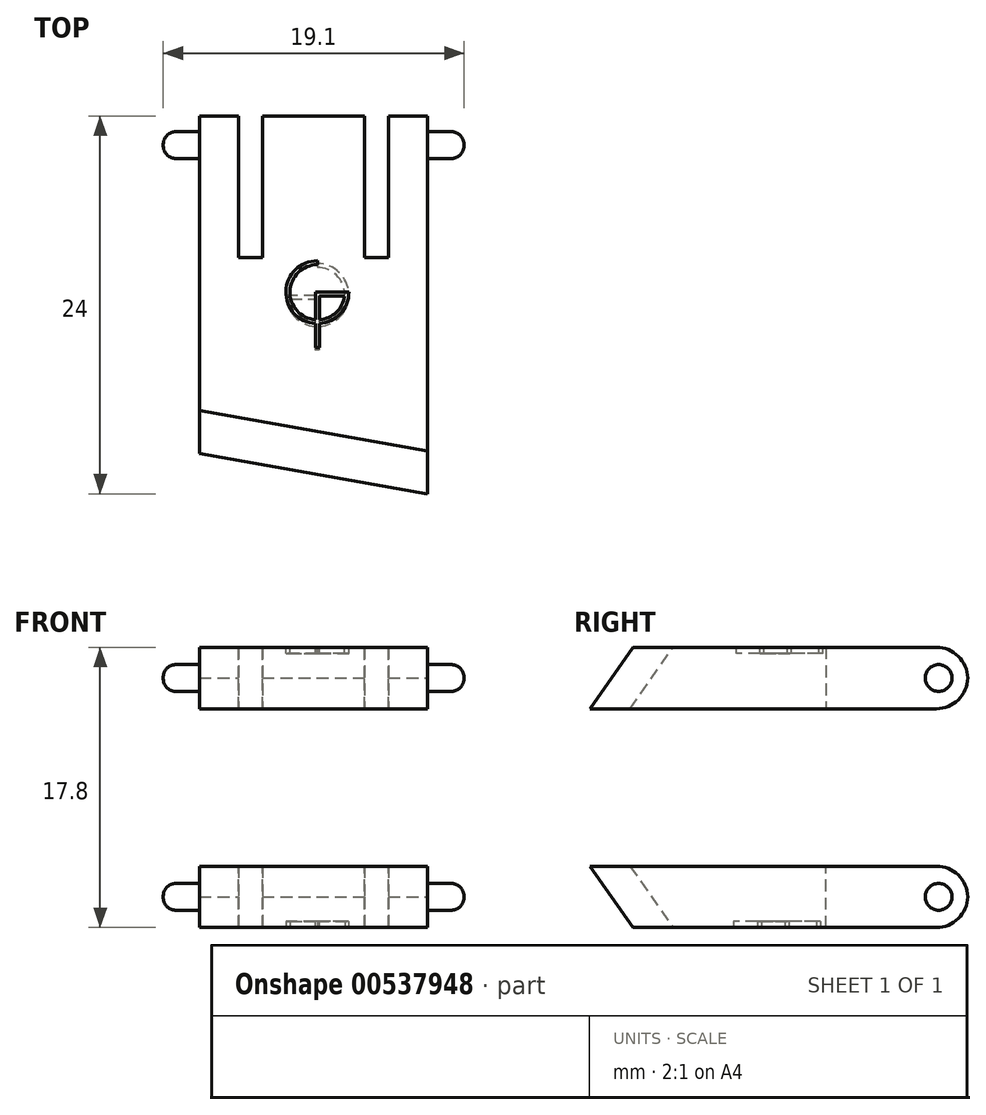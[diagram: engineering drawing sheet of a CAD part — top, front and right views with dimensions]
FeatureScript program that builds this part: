
annotation { "Feature Type Name" : "Feature", "Feature Type Description" : "" }
export const myFeature = defineFeature(function(context is Context, id is Id, definition is map)
    precondition{}
    {
        {
            var Q0;
            Q0=qCreatedBy(makeId("Top.planeOp"),FACE);
            var sketch = newSketch(context, id + "F0", { "sketchPlane" : qUnion([Q0])});
            skLineSegment(sketch, "E0", {"start": v(0, 0) * mm, "end": v(-14.5, 2.56) * mm});
            skLineSegment(sketch, "E1", {"start": v(-14.5, 2.56) * mm, "end": v(-14.5, 24) * mm});
            skLineSegment(sketch, "E2", {"start": v(-14.5, 24) * mm, "end": v(0, 24) * mm});
            skLineSegment(sketch, "E3", {"start": v(0, 24) * mm, "end": v(0, 0) * mm});
            skLineSegment(sketch, "E4.bottom", {"start": v(-12, 24) * mm, "end": v(-10.5, 24) * mm});
            skLineSegment(sketch, "E4.top", {"start": v(-12, 15) * mm, "end": v(-10.5, 15) * mm});
            skLineSegment(sketch, "E4.left", {"start": v(-12, 24) * mm, "end": v(-12, 15) * mm});
            skLineSegment(sketch, "E4.right", {"start": v(-10.5, 24) * mm, "end": v(-10.5, 15) * mm});
            skLineSegment(sketch, "E5.bottom", {"start": v(-2.5, 24) * mm, "end": v(-4, 24) * mm});
            skLineSegment(sketch, "E5.top", {"start": v(-2.5, 15) * mm, "end": v(-4, 15) * mm});
            skLineSegment(sketch, "E5.left", {"start": v(-2.5, 24) * mm, "end": v(-2.5, 15) * mm});
            skLineSegment(sketch, "E5.right", {"start": v(-4, 24) * mm, "end": v(-4, 15) * mm});
            skSolve(sketch);
        }
        {
            var Q0;
            Q0=makeQuery(id+"F0.imprint","IMPRINT",FACE,{"disambiguationData":[TD([[makeQuery(id+"F0.imprint","IMPRINT",EDGE,{"derivedFrom":sQuery(id+"F0.wireOp",EDGE,"E0")}),-1.0]])]});
            var Q1;
            {var subQ1=sQuery(id+"F0.wireOp",EDGE,"c5bb8d40-925b-485c-b122-8afd0081a890");Q1=makeQuery(id+"F0.imprint","IMPRINT",FACE,{"disambiguationData":[TD([[makeQuery(id+"F0.imprint","IMPRINT",EDGE,{"derivedFrom":subQ1}),1.0]])]});}
            var Q2;
            {var subQ0=sQuery(id+"F0.wireOp",EDGE,"f95112e1-4d56-459a-80a0-04d841074a68");Q2=makeQuery(id+"F0.imprint","IMPRINT",FACE,{"disambiguationData":[TD([[makeQuery(id+"F0.imprint","IMPRINT",EDGE,{"derivedFrom":subQ0}),1.0]])]});}
            var Q3;
            {var subQ1=sQuery(id+"F0.wireOp",EDGE,"91befa4d-aa7f-4066-8ede-e3ff8ab19f0f");Q3=makeQuery(id+"F0.imprint","IMPRINT",FACE,{"disambiguationData":[TD([[makeQuery(id+"F0.imprint","IMPRINT",EDGE,{"derivedFrom":subQ1}),1.0]])]});}
            var Q4;
            {var subQ5=sQuery(id+"F0.wireOp",EDGE,"8b45276f-696a-430b-a867-6ecf755f5e75");Q4=makeQuery(id+"F0.imprint","IMPRINT",FACE,{"disambiguationData":[TD([[makeQuery(id+"F0.imprint","IMPRINT",EDGE,{"derivedFrom":subQ5}),1.0]])]});}
            var Q5;
            {var subQ0=sQuery(id+"F0.wireOp",EDGE,"857528f7-3fc0-4300-9383-177ff648e449");var subQ1=sQuery(id+"F0.wireOp",EDGE,"b7ffc7d4-f97f-4348-9500-127a82e465bb");var subQ2=makeQuery(id+"F0.imprint","INTERSECT",VERTEX,{"derivedFrom":[subQ1,subQ0]});Q5=makeQuery(id+"F0.imprint","IMPRINT",FACE,{"disambiguationData":[TD([[makeQuery(id+"F0.imprint","IMPRINT",EDGE,{"disambiguationData":[TD([[subQ2,-1.0]])],"derivedFrom":subQ1}),1.0]])]});}
            var Q6;
            {var subQ0=sQuery(id+"F0.wireOp",EDGE,"2bfb2500-52ae-434e-aba9-8a9b67f69133");Q6=makeQuery(id+"F0.imprint","IMPRINT",FACE,{"disambiguationData":[TD([[makeQuery(id+"F0.imprint","IMPRINT",EDGE,{"derivedFrom":subQ0}),-1.0]])]});}
            extrude(context, id + "F1", {"entities" : qUnion([Q0, Q1, Q2, Q3, Q4, Q5, Q6]), "depth" : 3.9 * mm, "offsetDistance" : 25 * mm});
        }
        {
            var Q0;
            Q0=makeQuery(id+"F1.opExtrude","SWEPT_FACE",FACE,{"disambiguationData":[OSD([sQuery(id+"F0.wireOp",EDGE,"E3")])]});
            var sketch = newSketch(context, id + "F2", { "sketchPlane" : qUnion([Q0])});
            skCircle(sketch, "E6", {"center": v(22.15, 1.95) * mm, "radius": 0.85 * mm});
            skPoint(sketch, "E6.centerSnap0", {"position": v(24, 1.95) * mm});
            skSolve(sketch);
        }
        {
            var Q0;
            Q0 = qSketchRegion(id + "F2", true);
            extrude(context, id + "F3", {"entities" : qUnion([Q0]), "operationType" : NewBodyOperationType.ADD, "depth" : 2.3 * mm, "offsetDistance" : 25 * mm});
        }
        {
            var Q0;
            Q0=makeQuery(id+"F1.opExtrude","SWEPT_FACE",FACE,{"disambiguationData":[OSD([sQuery(id+"F0.wireOp",EDGE,"E1")])]});
            var sketch = newSketch(context, id + "F4", { "sketchPlane" : qUnion([Q0])});
            skCircle(sketch, "E7", {"center": v(-22.15, 1.95) * mm, "radius": 0.85 * mm});
            skPoint(sketch, "E7.centerSnap0", {"position": v(-24, 1.95) * mm});
            skSolve(sketch);
        }
        {
            var Q0;
            Q0=makeQuery(id+"F4.imprint","IMPRINT",FACE,{"disambiguationData":[TD([[makeQuery(id+"F4.imprint","IMPRINT",EDGE,{"derivedFrom":sQuery(id+"F4.wireOp",EDGE,"E7")}),1.0]])]});
            extrude(context, id + "F5", {"entities" : qUnion([Q0]), "operationType" : NewBodyOperationType.ADD, "depth" : 2.3 * mm, "offsetDistance" : 25 * mm});
        }
        {
            var Q0;
            Q0=makeQuery(id+"F3.opExtrude","CAP_FACE",FACE,{"disambiguationData":[OSD([sQuery(id+"F2.wireOp",EDGE,"E6")])],"isStart":false});
            var Q1;
            Q1=makeQuery(id+"F5.opExtrude","CAP_FACE",FACE,{"disambiguationData":[OSD([sQuery(id+"F4.wireOp",EDGE,"E7")])],"isStart":false});
            fillet(context, id + "F6", {"entities" : qUnion([Q0, Q1]), "radius" : .8 * mm, "allowEdgeOverflow" : false});
        }
        {
            var Q0;
            {var subQ0=sQuery(id+"F0.wireOp",EDGE,"E2");Q0=makeQuery(id+"F1.opExtrude","CAP_EDGE",EDGE,{"disambiguationData":[OSD([subQ0]),TDD([makeQuery(id+"F0.imprint","IMPRINT",EDGE,{"disambiguationData":[TD([[makeQuery(id+"F0.imprint","INTERSECT",VERTEX,{"derivedFrom":[subQ0,sQuery(id+"F0.wireOp",EDGE,"E4.bottom"),sQuery(id+"F0.wireOp",EDGE,"E4.right")]}),-1.0]])],"derivedFrom":subQ0})])],"isStart":false});}
            var Q1;
            {var subQ0=sQuery(id+"F0.wireOp",EDGE,"E2");Q1=makeQuery(id+"F1.opExtrude","CAP_EDGE",EDGE,{"disambiguationData":[OSD([subQ0]),TDD([makeQuery(id+"F0.imprint","IMPRINT",EDGE,{"disambiguationData":[TD([[makeQuery(id+"F0.imprint","INTERSECT",VERTEX,{"derivedFrom":[sQuery(id+"F0.wireOp",EDGE,"E1"),subQ0]}),-1.0]])],"derivedFrom":subQ0})])],"isStart":false});}
            var Q2;
            {var subQ0=sQuery(id+"F0.wireOp",EDGE,"E2");Q2=makeQuery(id+"F1.opExtrude","CAP_EDGE",EDGE,{"disambiguationData":[OSD([subQ0]),TDD([makeQuery(id+"F0.imprint","IMPRINT",EDGE,{"disambiguationData":[TD([[makeQuery(id+"F0.imprint","INTERSECT",VERTEX,{"derivedFrom":[subQ0,sQuery(id+"F0.wireOp",EDGE,"E3")]}),1.0]])],"derivedFrom":subQ0})])],"isStart":false});}
            var Q3;
            {var subQ0=sQuery(id+"F0.wireOp",EDGE,"E2");Q3=makeQuery(id+"F1.opExtrude","CAP_EDGE",EDGE,{"disambiguationData":[OSD([subQ0]),TDD([makeQuery(id+"F0.imprint","IMPRINT",EDGE,{"disambiguationData":[TD([[makeQuery(id+"F0.imprint","INTERSECT",VERTEX,{"derivedFrom":[subQ0,sQuery(id+"F0.wireOp",EDGE,"E3")]}),1.0]])],"derivedFrom":subQ0})])],"isStart":true});}
            var Q4;
            {var subQ0=sQuery(id+"F0.wireOp",EDGE,"E2");Q4=makeQuery(id+"F1.opExtrude","CAP_EDGE",EDGE,{"disambiguationData":[OSD([subQ0]),TDD([makeQuery(id+"F0.imprint","IMPRINT",EDGE,{"disambiguationData":[TD([[makeQuery(id+"F0.imprint","INTERSECT",VERTEX,{"derivedFrom":[subQ0,sQuery(id+"F0.wireOp",EDGE,"E4.bottom"),sQuery(id+"F0.wireOp",EDGE,"E4.right")]}),-1.0]])],"derivedFrom":subQ0})])],"isStart":true});}
            var Q5;
            {var subQ0=sQuery(id+"F0.wireOp",EDGE,"E2");Q5=makeQuery(id+"F1.opExtrude","CAP_EDGE",EDGE,{"disambiguationData":[OSD([subQ0]),TDD([makeQuery(id+"F0.imprint","IMPRINT",EDGE,{"disambiguationData":[TD([[makeQuery(id+"F0.imprint","INTERSECT",VERTEX,{"derivedFrom":[sQuery(id+"F0.wireOp",EDGE,"E1"),subQ0]}),-1.0]])],"derivedFrom":subQ0})])],"isStart":true});}
            fillet(context, id + "F7", {"entities" : qUnion([Q0, Q1, Q2, Q3, Q4, Q5]), "radius" : 2 * mm, "allowEdgeOverflow" : false});
        }
        {
            var Q0;
            Q0=makeQuery(id+"F1.opExtrude","SWEPT_FACE",FACE,{"disambiguationData":[OSD([sQuery(id+"F0.wireOp",EDGE,"E3")])]});
            var sketch = newSketch(context, id + "F8", { "sketchPlane" : qUnion([Q0])});
            skLineSegment(sketch, "E8", {"start": v(0, 0) * mm, "end": v(2.73, 3.9) * mm});
            skLineSegment(sketch, "E9", {"start": v(2.73, 3.9) * mm, "end": v(0, 3.9) * mm});
            skLineSegment(sketch, "E10", {"start": v(0, 3.9) * mm, "end": v(0, 0) * mm});
            skSolve(sketch);
        }
        {
            var Q0;
            Q0=makeQuery(id+"F8.imprint","IMPRINT",FACE,{"disambiguationData":[TD([[makeQuery(id+"F8.imprint","IMPRINT",EDGE,{"derivedFrom":sQuery(id+"F8.wireOp",EDGE,"E8")}),1.0]])]});
            var Q1;
            Q1=makeQuery(id+"F1.opExtrude","CAP_EDGE",EDGE,{"disambiguationData":[OSD([sQuery(id+"F0.wireOp",EDGE,"E0")])],"isStart":false});
            sweep(context, id + "F9", {"operationType" : NewBodyOperationType.REMOVE, "profiles" : qUnion([Q0]), "path" : qUnion([Q1])});
        }
        {
            var Q0;
            Q0=makeQuery(id+"F1.opExtrude","SWEPT_BODY",BODY,{"disambiguationData":[OSD([sQuery(id+"F0.wireOp",EDGE,"E0"),sQuery(id+"F0.wireOp",EDGE,"E1"),sQuery(id+"F0.wireOp",EDGE,"E2"),sQuery(id+"F0.wireOp",EDGE,"E3"),sQuery(id+"F0.wireOp",EDGE,"E4.top"),sQuery(id+"F0.wireOp",EDGE,"E4.left"),sQuery(id+"F0.wireOp",EDGE,"E4.right"),sQuery(id+"F0.wireOp",EDGE,"E5.top"),sQuery(id+"F0.wireOp",EDGE,"E5.left"),sQuery(id+"F0.wireOp",EDGE,"E5.right")])]});
            transform(context, id + "F10", {"entities" : qUnion([Q0]), "transformType" : TransformType.TRANSLATION_3D, "dx" : 0 * mm, "dy" : 0 * mm, "dz" : 5 * mm, "makeCopy" : false});
        }
        {
            var Q0;
            Q0=makeQuery(id+"F1.opExtrude","SWEPT_BODY",BODY,{"disambiguationData":[OSD([sQuery(id+"F0.wireOp",EDGE,"E0"),sQuery(id+"F0.wireOp",EDGE,"E1"),sQuery(id+"F0.wireOp",EDGE,"E2"),sQuery(id+"F0.wireOp",EDGE,"E3"),sQuery(id+"F0.wireOp",EDGE,"E4.top"),sQuery(id+"F0.wireOp",EDGE,"E4.left"),sQuery(id+"F0.wireOp",EDGE,"E4.right"),sQuery(id+"F0.wireOp",EDGE,"E5.top"),sQuery(id+"F0.wireOp",EDGE,"E5.left"),sQuery(id+"F0.wireOp",EDGE,"E5.right")])]});
            var Q1;
            Q1=qCreatedBy(makeId("Top.planeOp"),FACE);
            mirror(context, id + "F11", {"entities" : qUnion([Q0]), "mirrorPlane" : qUnion([Q1])});
        }
        {
            var Q0;
            Q0=makeQuery(id+"F1.opExtrude","CAP_FACE",FACE,{"disambiguationData":[OSD([sQuery(id+"F0.wireOp",EDGE,"E0"),sQuery(id+"F0.wireOp",EDGE,"E1"),sQuery(id+"F0.wireOp",EDGE,"E2"),sQuery(id+"F0.wireOp",EDGE,"E3"),sQuery(id+"F0.wireOp",EDGE,"E4.top"),sQuery(id+"F0.wireOp",EDGE,"E4.left"),sQuery(id+"F0.wireOp",EDGE,"E4.right"),sQuery(id+"F0.wireOp",EDGE,"E5.top"),sQuery(id+"F0.wireOp",EDGE,"E5.left"),sQuery(id+"F0.wireOp",EDGE,"E5.right")])],"isStart":false});
            var sketch = newSketch(context, id + "F12", { "sketchPlane" : qUnion([Q0])});
            skLineSegment(sketch, "E11.bottom", {"start": v(-7, 14.8) * mm, "end": v(-5, 14.8) * mm, "construction": true});
            skLineSegment(sketch, "E11.top", {"start": v(-7, 12.8) * mm, "end": v(-5, 12.8) * mm, "construction": true});
            skLineSegment(sketch, "E11.left", {"start": v(-7, 14.8) * mm, "end": v(-7, 12.8) * mm, "construction": true});
            skLineSegment(sketch, "E11.right", {"start": v(-5, 14.8) * mm, "end": v(-5, 12.8) * mm, "construction": true});
            skArc(sketch, "E12", {"start": v(-7, 14.8) * mm, "mid": v(-8.42, 11.4) * mm, "end": v(-5, 12.8) * mm});
            skLineSegment(sketch, "E13", {"start": v(-7, 14.8) * mm, "end": v(-7, 14.55) * mm});
            skLineSegment(sketch, "E14", {"start": v(-5, 12.8) * mm, "end": v(-5.26, 12.8) * mm});
            skArc(sketch, "E15", {"start": v(-7, 14.55) * mm, "mid": v(-8.24, 11.57) * mm, "end": v(-5.26, 12.8) * mm});
            skLineSegment(sketch, "E16", {"start": v(-5.26, 12.8) * mm, "end": v(-7.13, 12.8) * mm});
            skLineSegment(sketch, "E17", {"start": v(-7.13, 12.8) * mm, "end": v(-7.13, 9.3) * mm});
            skLineSegment(sketch, "E18", {"start": v(-7.13, 9.3) * mm, "end": v(-6.88, 9.3) * mm});
            skLineSegment(sketch, "E19", {"start": v(-5.27, 12.55) * mm, "end": v(-6.88, 12.55) * mm});
            skLineSegment(sketch, "E20", {"start": v(-6.88, 12.55) * mm, "end": v(-6.88, 9.3) * mm});
            skSolve(sketch);
        }
        {
            var Q0;
            {var subQ0=sQuery(id+"F12.wireOp",EDGE,"E13");Q0=makeQuery(id+"F12.imprint","IMPRINT",FACE,{"disambiguationData":[TD([[makeQuery(id+"F12.imprint","IMPRINT",EDGE,{"derivedFrom":subQ0}),-1.0]])]});}
            var Q1;
            {var subQ1=sQuery(id+"F12.wireOp",EDGE,"E14");Q1=makeQuery(id+"F12.imprint","IMPRINT",FACE,{"disambiguationData":[TD([[makeQuery(id+"F12.imprint","IMPRINT",EDGE,{"derivedFrom":subQ1}),1.0]])]});}
            var Q2;
            {var subQ1=sQuery(id+"F12.wireOp",EDGE,"E16");Q2=makeQuery(id+"F12.imprint","IMPRINT",FACE,{"disambiguationData":[TD([[makeQuery(id+"F12.imprint","IMPRINT",EDGE,{"derivedFrom":subQ1}),1.0]])]});}
            var Q3;
            {var subQ0=sQuery(id+"F12.wireOp",EDGE,"E17");var subQ1=sQuery(id+"F12.wireOp",EDGE,"E12");var subQ2=makeQuery(id+"F12.imprint","INTERSECT",VERTEX,{"derivedFrom":[subQ1,subQ0]});Q3=makeQuery(id+"F12.imprint","IMPRINT",FACE,{"disambiguationData":[TD([[makeQuery(id+"F12.imprint","IMPRINT",EDGE,{"disambiguationData":[TD([[subQ2,-1.0]])],"derivedFrom":subQ1}),1.0]])]});}
            var Q4;
            {var subQ5=sQuery(id+"F12.wireOp",EDGE,"E18");Q4=makeQuery(id+"F12.imprint","IMPRINT",FACE,{"disambiguationData":[TD([[makeQuery(id+"F12.imprint","IMPRINT",EDGE,{"derivedFrom":subQ5}),1.0]])]});}
            extrude(context, id + "F13", {"entities" : qUnion([Q0, Q1, Q2, Q3, Q4]), "operationType" : NewBodyOperationType.REMOVE, "oppositeDirection" : true, "depth" : .4 * mm, "offsetDistance" : 25 * mm});
        }
        {
            var Q0;
            Q0=makeQuery(id+"F11.opPattern","COPY",FACE,{"derivedFrom":makeQuery(id+"F1.opExtrude","CAP_FACE",FACE,{"disambiguationData":[OSD([sQuery(id+"F0.wireOp",EDGE,"E0"),sQuery(id+"F0.wireOp",EDGE,"E1"),sQuery(id+"F0.wireOp",EDGE,"E2"),sQuery(id+"F0.wireOp",EDGE,"E3"),sQuery(id+"F0.wireOp",EDGE,"E4.top"),sQuery(id+"F0.wireOp",EDGE,"E4.left"),sQuery(id+"F0.wireOp",EDGE,"E4.right"),sQuery(id+"F0.wireOp",EDGE,"E5.top"),sQuery(id+"F0.wireOp",EDGE,"E5.left"),sQuery(id+"F0.wireOp",EDGE,"E5.right")])],"isStart":false}),"instanceName":"1"});
            var sketch = newSketch(context, id + "F14", { "sketchPlane" : qUnion([Q0])});
            skLineSegment(sketch, "E21.bottom", {"start": v(-7.01, -14.63) * mm, "end": v(-9.01, -14.63) * mm, "construction": true});
            skLineSegment(sketch, "E21.top", {"start": v(-7.01, -12.63) * mm, "end": v(-9.01, -12.63) * mm, "construction": true});
            skLineSegment(sketch, "E21.left", {"start": v(-7.01, -14.63) * mm, "end": v(-7.01, -12.63) * mm, "construction": true});
            skLineSegment(sketch, "E21.right", {"start": v(-9.01, -14.63) * mm, "end": v(-9.01, -12.63) * mm, "construction": true});
            skArc(sketch, "E22", {"start": v(-7.01, -14.63) * mm, "mid": v(-5.6, -11.22) * mm, "end": v(-9.01, -12.63) * mm});
            skLineSegment(sketch, "E23", {"start": v(-7.01, -14.63) * mm, "end": v(-7.01, -14.38) * mm});
            skLineSegment(sketch, "E24", {"start": v(-9.01, -12.63) * mm, "end": v(-8.76, -12.63) * mm});
            skArc(sketch, "E25", {"start": v(-7.01, -14.38) * mm, "mid": v(-5.78, -11.4) * mm, "end": v(-8.76, -12.63) * mm});
            skLineSegment(sketch, "E26", {"start": v(-8.76, -12.63) * mm, "end": v(-6.9, -12.63) * mm});
            skLineSegment(sketch, "E27", {"start": v(-6.9, -12.63) * mm, "end": v(-6.9, -9.13) * mm});
            skLineSegment(sketch, "E28", {"start": v(-6.9, -9.13) * mm, "end": v(-7.14, -9.13) * mm});
            skLineSegment(sketch, "E29", {"start": v(-8.75, -12.38) * mm, "end": v(-7.14, -12.38) * mm});
            skLineSegment(sketch, "E30", {"start": v(-7.14, -12.38) * mm, "end": v(-7.14, -9.13) * mm});
            skSolve(sketch);
        }
        {
            var Q0;
            {var subQ0=sQuery(id+"F14.wireOp",EDGE,"E23");Q0=makeQuery(id+"F14.imprint","IMPRINT",FACE,{"disambiguationData":[TD([[makeQuery(id+"F14.imprint","IMPRINT",EDGE,{"derivedFrom":subQ0}),-1.0]])]});}
            var Q1;
            {var subQ1=sQuery(id+"F14.wireOp",EDGE,"E26");Q1=makeQuery(id+"F14.imprint","IMPRINT",FACE,{"disambiguationData":[TD([[makeQuery(id+"F14.imprint","IMPRINT",EDGE,{"derivedFrom":subQ1}),1.0]])]});}
            var Q2;
            {var subQ1=sQuery(id+"F14.wireOp",EDGE,"E24");Q2=makeQuery(id+"F14.imprint","IMPRINT",FACE,{"disambiguationData":[TD([[makeQuery(id+"F14.imprint","IMPRINT",EDGE,{"derivedFrom":subQ1}),1.0]])]});}
            var Q3;
            {var subQ0=sQuery(id+"F14.wireOp",EDGE,"E27");var subQ1=sQuery(id+"F14.wireOp",EDGE,"E22");var subQ2=makeQuery(id+"F14.imprint","INTERSECT",VERTEX,{"derivedFrom":[subQ1,subQ0]});Q3=makeQuery(id+"F14.imprint","IMPRINT",FACE,{"disambiguationData":[TD([[makeQuery(id+"F14.imprint","IMPRINT",EDGE,{"disambiguationData":[TD([[subQ2,-1.0]])],"derivedFrom":subQ1}),1.0]])]});}
            var Q4;
            {var subQ5=sQuery(id+"F14.wireOp",EDGE,"E28");Q4=makeQuery(id+"F14.imprint","IMPRINT",FACE,{"disambiguationData":[TD([[makeQuery(id+"F14.imprint","IMPRINT",EDGE,{"derivedFrom":subQ5}),1.0]])]});}
            extrude(context, id + "F15", {"entities" : qUnion([Q0, Q1, Q2, Q3, Q4]), "operationType" : NewBodyOperationType.REMOVE, "oppositeDirection" : true, "depth" : .4 * mm, "offsetDistance" : 25 * mm});
        }
    });
